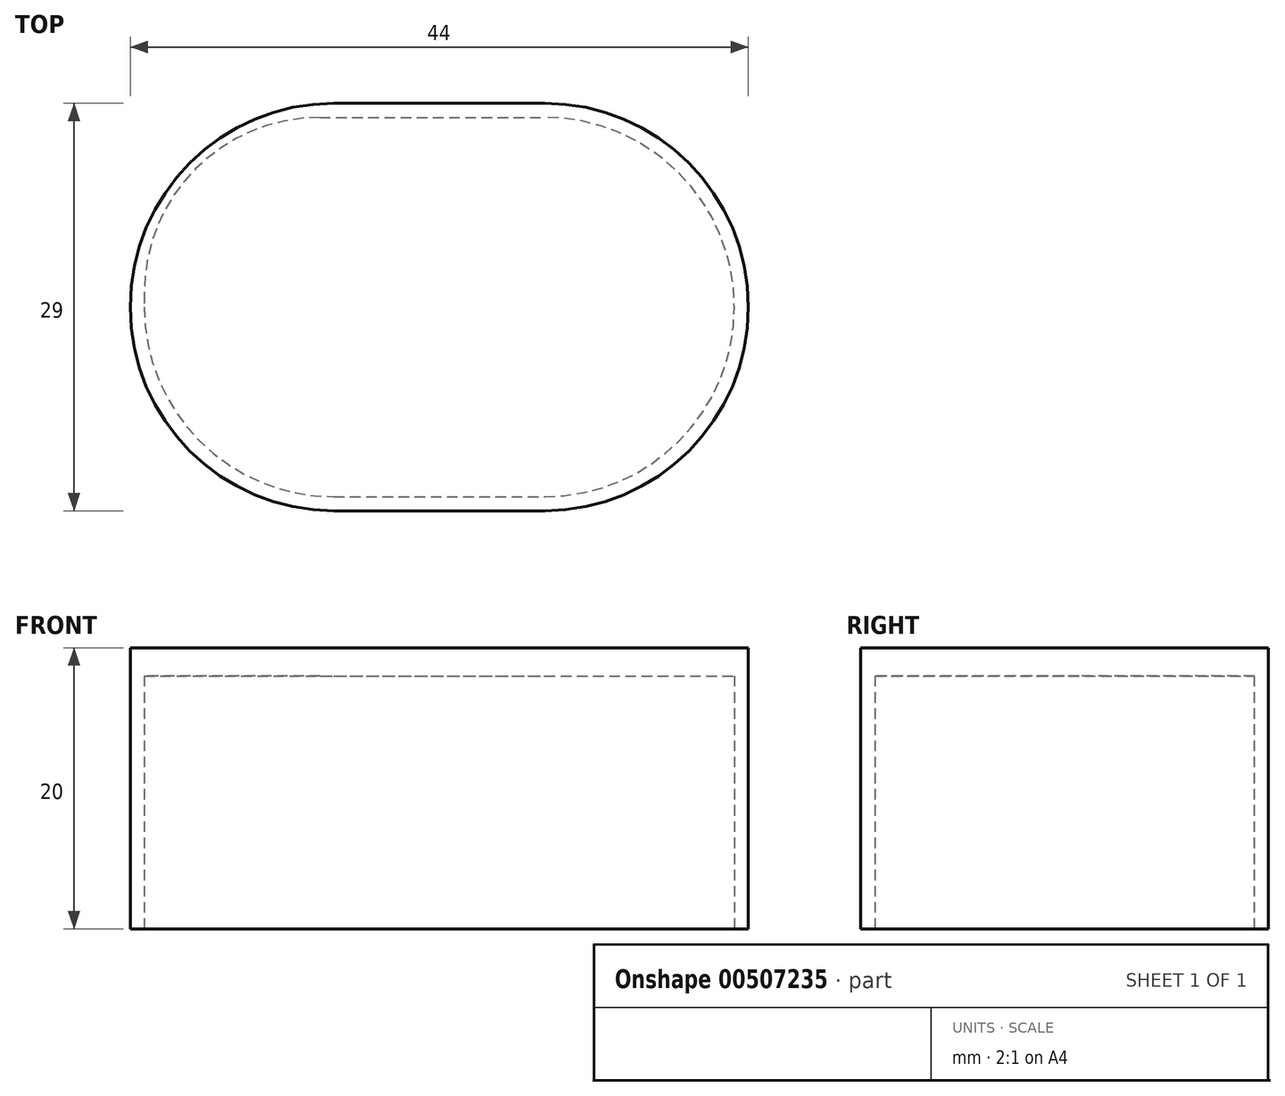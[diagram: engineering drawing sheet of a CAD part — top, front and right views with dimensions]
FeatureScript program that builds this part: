
annotation { "Feature Type Name" : "Feature", "Feature Type Description" : "" }
export const myFeature = defineFeature(function(context is Context, id is Id, definition is map)
    precondition{}
    {
        {
            var Q0;
            Q0=qCreatedBy(makeId("Top.planeOp"),FACE);
            var sketch = newSketch(context, id + "F0", { "sketchPlane" : qUnion([Q0])});
            skLineSegment(sketch, "E0.bottom", {"start": v(-8.5, 13.5) * mm, "end": v(7.5, 13.5) * mm});
            skLineSegment(sketch, "E0.top", {"start": v(-7.5, -13.5) * mm, "end": v(7.5, -13.5) * mm});
            skLineSegment(sketch, "E0.left", {"start": v(-21, 1) * mm, "end": v(-21, 0) * mm});
            skLineSegment(sketch, "E0.right", {"start": v(21, 0) * mm, "end": v(21, 0) * mm});
            skPoint(sketch, "E0.middle", {"position": v(0, 0) * mm});
            skPoint(sketch, "E1.visualSharp", {"position": v(-21, 13.5) * mm});
            skArc(sketch, "E1.filletArc", {"start": v(-8.5, 13.5) * mm, "mid": v(-17.34, 9.84) * mm, "end": v(-21, 1) * mm});
            skPoint(sketch, "E2.visualSharp", {"position": v(21, 13.5) * mm});
            skArc(sketch, "E2.filletArc", {"start": v(21, 0) * mm, "mid": v(17.05, 9.55) * mm, "end": v(7.5, 13.5) * mm});
            skPoint(sketch, "E3.visualSharp", {"position": v(21, -13.5) * mm});
            skArc(sketch, "E3.filletArc", {"start": v(7.5, -13.5) * mm, "mid": v(17.05, -9.55) * mm, "end": v(21, 0) * mm});
            skPoint(sketch, "E4.visualSharp", {"position": v(-21, -13.5) * mm});
            skArc(sketch, "E4.filletArc", {"start": v(-21, 0) * mm, "mid": v(-17.05, -9.55) * mm, "end": v(-7.5, -13.5) * mm});
            skSolve(sketch);
        }
        {
            var Q0;
            Q0=qCreatedBy(makeId("Top.planeOp"),FACE);
            var sketch = newSketch(context, id + "F1", { "sketchPlane" : qUnion([Q0])});
            skLineSegment(sketch, "E5.bottom", {"start": v(-7.5, 14.5) * mm, "end": v(7.5, 14.5) * mm});
            skLineSegment(sketch, "E5.top", {"start": v(-7.5, -14.5) * mm, "end": v(7.5, -14.5) * mm});
            skLineSegment(sketch, "E5.left", {"start": v(-22, 0) * mm, "end": v(-22, 0) * mm});
            skLineSegment(sketch, "E5.right", {"start": v(22, 0) * mm, "end": v(22, 0) * mm});
            skPoint(sketch, "E5.middle", {"position": v(0, 0) * mm});
            skPoint(sketch, "E6.visualSharp", {"position": v(-22, 14.5) * mm});
            skArc(sketch, "E6.filletArc", {"start": v(-7.5, 14.5) * mm, "mid": v(-17.75, 10.25) * mm, "end": v(-22, 0) * mm});
            skPoint(sketch, "E7.visualSharp", {"position": v(22, 14.5) * mm});
            skArc(sketch, "E7.filletArc", {"start": v(22, 0) * mm, "mid": v(17.75, 10.25) * mm, "end": v(7.5, 14.5) * mm});
            skPoint(sketch, "E8.visualSharp", {"position": v(22, -14.5) * mm});
            skArc(sketch, "E8.filletArc", {"start": v(7.5, -14.5) * mm, "mid": v(17.75, -10.25) * mm, "end": v(22, 0) * mm});
            skPoint(sketch, "E9.visualSharp", {"position": v(-22, -14.5) * mm});
            skArc(sketch, "E9.filletArc", {"start": v(-22, 0) * mm, "mid": v(-17.75, -10.25) * mm, "end": v(-7.5, -14.5) * mm});
            skSolve(sketch);
        }
        {
            var Q0;
            Q0 = qSketchRegion(id + "F1", true);
            extrude(context, id + "F2", {"entities" : qUnion([Q0]), "depth" : 20 * mm});
        }
        {
            var Q0;
            Q0 = qSketchRegion(id + "F0", true);
            extrude(context, id + "F3", {"entities" : qUnion([Q0]), "operationType" : NewBodyOperationType.REMOVE, "depth" : 18 * mm});
        }
    });
